# Revit family: Albardilla MB remate IZQ. C-1
name_source: partatom
category: Modelos genéricos
units: mm (PartAtom-declared; Revit-internal decimal feet)

## family parameters
Compartido = No
Corte con vacíos al cargar = No
Cota de conector redondo = Diámetro de uso
Puede alojar armadura = No
Punto de cálculo de habitación = No
Se basa en plano de trabajo = No
Siempre vertical = No
Tipo de pieza = Normal

## types (10) — shared parameters
Descripción = Pieza de hormigón polímero con anclaje de acero inoxidable.
Fabricante = ULMA Architectural Solutions
Material = Hormigón polímero STONEO. Color C-1
URL = https://www.ulmaarchitectural.com
zero-valued in all types: Elevación por defecto

## per-type parameters (varying)
| type | Ancho | Ancho doble | Ancho total | Modelo | Visible dos líneas | Visible una linea |
| RIMB12 | 120 mm  [stored 0.393701 ft] | 30 mm  [stored 0.0984252 ft] | 170 mm  [stored 0.557743 ft] | Albardilla MB12 remate izquierda | No | Sí |
| RIMB14 | 140 mm  [stored 0.459318 ft] | 35 mm  [stored 0.114829 ft] | 190 mm | Albardilla MB14 remate izquierda | No | Sí |
| RIMB17 | 170 mm  [stored 0.557743 ft] | 43 mm | 220 mm  [stored 0.721785 ft] | Albardilla MB17 remate izquierda | No | Sí |
| RIMB19 | 190 mm | 48 mm | 240 mm  [stored 0.787402 ft] | Albardilla MB19 remate izquierda | No | Sí |
| RIMB22 | 220 mm  [stored 0.721785 ft] | 55 mm  [stored 0.180446 ft] | 270 mm  [stored 0.885827 ft] | Albardilla MB22 remate izquierda | No | Sí |
| RIMB25 | 250 mm  [stored 0.82021 ft] | 63 mm | 300 mm | Albardilla MB25 remate izquierda | No | Sí |
| RIMB30 | 300 mm | 75 mm | 350 mm  [stored 1.14829 ft] | Albardilla MB30 remate izquierda | No | Sí |
| RIMB35 | 350 mm  [stored 1.14829 ft] | 88 mm | 400 mm  [stored 1.31234 ft] | Albardilla MB35 remate izquierda | Sí | No |
| RIMB40 | 400 mm  [stored 1.31234 ft] | 100 mm  [stored 0.328084 ft] | 450 mm  [stored 1.47638 ft] | Albardilla MB40 remate izquierda | Sí | No |
| RIMB27 | 270 mm  [stored 0.885827 ft] | 68 mm | 320 mm  [stored 1.04987 ft] | Albardilla MB27 remate izquierda | No | Sí |

note: column(s) folded — value = type name in every type: Código de montaje

note: [stored X ft] marks values corroborated as IEEE doubles in the binary element streams (Revit-internal decimal feet)
